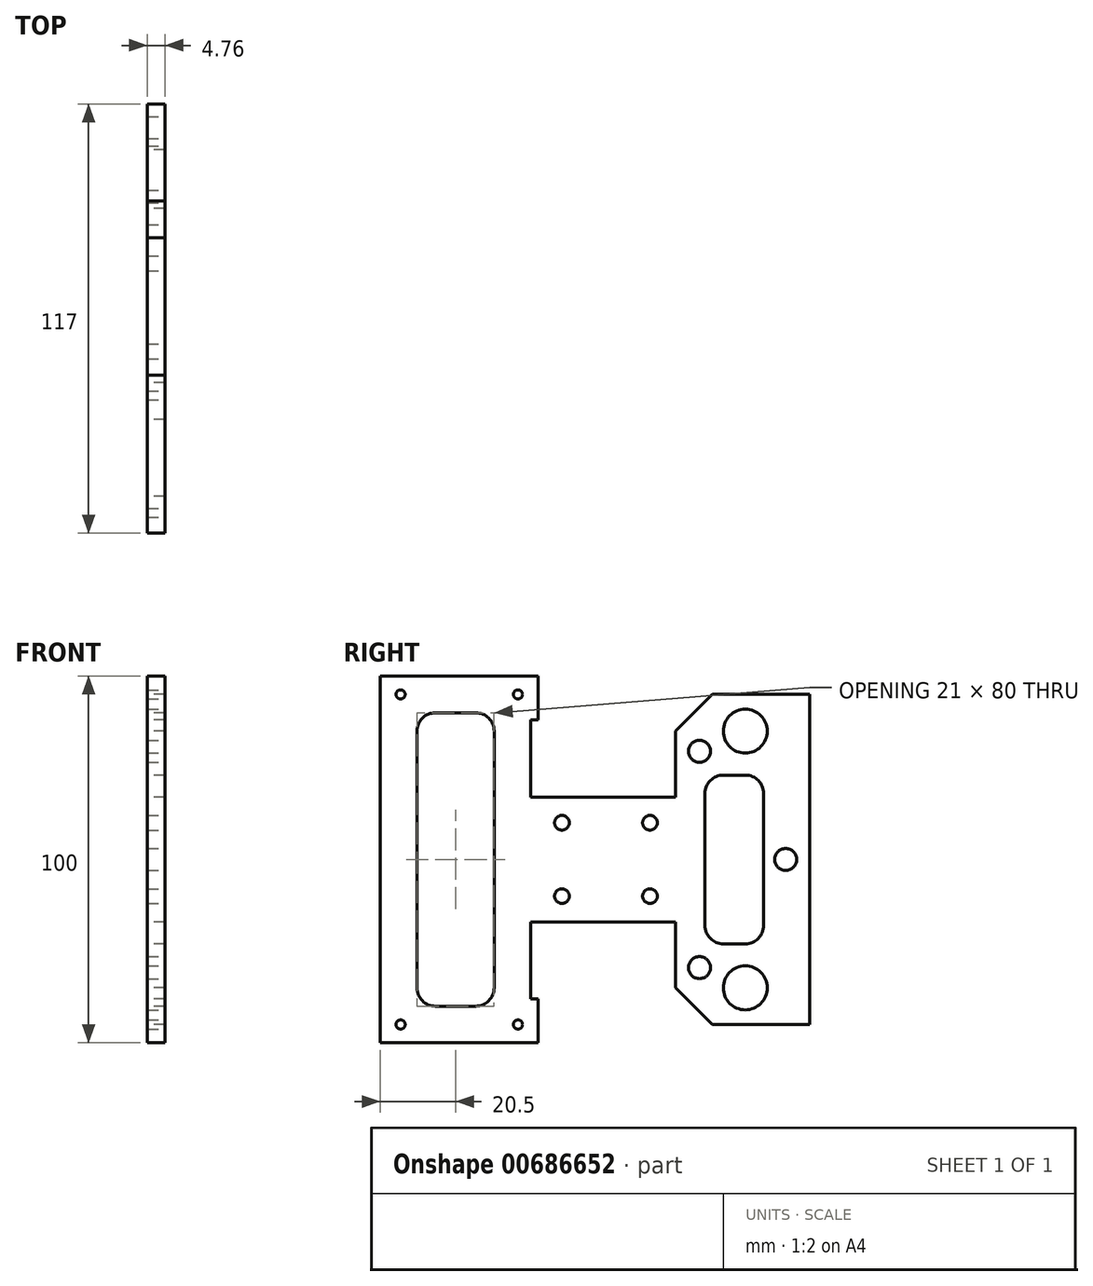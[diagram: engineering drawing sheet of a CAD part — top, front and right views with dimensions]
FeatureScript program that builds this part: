
annotation { "Feature Type Name" : "Feature", "Feature Type Description" : "" }
export const myFeature = defineFeature(function(context is Context, id is Id, definition is map)
    precondition{}
    {
        {
            var Q0;
            Q0=qCreatedBy(makeId("Right.planeOp"),FACE);
            var sketch = newSketch(context, id + "F0", { "sketchPlane" : qUnion([Q0])});
            skLineSegment(sketch, "E0.bottom", {"start": v(58.5, 17) * mm, "end": v(-58.5, 17) * mm});
            skLineSegment(sketch, "E0.top", {"start": v(58.5, -17) * mm, "end": v(-58.5, -17) * mm});
            skLineSegment(sketch, "E0.left", {"start": v(58.5, 17) * mm, "end": v(58.5, -17) * mm});
            skLineSegment(sketch, "E0.right", {"start": v(-58.5, 17) * mm, "end": v(-58.5, -17) * mm});
            skPoint(sketch, "E0.middle", {"position": v(0, 0) * mm});
            skLineSegment(sketch, "E1.bottom", {"start": v(-58.5, 17) * mm, "end": v(-17.5, 17) * mm, "construction": true});
            skLineSegment(sketch, "E1.top", {"start": v(-58.5, 38) * mm, "end": v(-17.5, 38) * mm, "construction": true});
            skLineSegment(sketch, "E1.left", {"start": v(-58.5, 17) * mm, "end": v(-58.5, 38) * mm});
            skLineSegment(sketch, "E1.right", {"start": v(-17.5, 17) * mm, "end": v(-17.5, 38) * mm});
            skLineSegment(sketch, "E2.bottom", {"start": v(-17.5, 38) * mm, "end": v(-15.5, 38) * mm});
            skLineSegment(sketch, "E2.top", {"start": v(-58.5, 50) * mm, "end": v(-15.5, 50) * mm});
            skLineSegment(sketch, "E2.left", {"start": v(-58.5, 38) * mm, "end": v(-58.5, 50) * mm});
            skLineSegment(sketch, "E2.right", {"start": v(-15.5, 38) * mm, "end": v(-15.5, 50) * mm});
            skLineSegment(sketch, "E3.bottom", {"start": v(58.5, 17) * mm, "end": v(22, 17) * mm});
            skLineSegment(sketch, "E3.top", {"start": v(58.5, 45) * mm, "end": v(32, 45) * mm});
            skLineSegment(sketch, "E3.left", {"start": v(58.5, 17) * mm, "end": v(58.5, 45) * mm});
            skLineSegment(sketch, "E3.right", {"start": v(22, 17) * mm, "end": v(22, 35) * mm});
            skLineSegment(sketch, "E4", {"start": v(22, 35) * mm, "end": v(32, 45) * mm});
            skLineSegment(sketch, "E5.bottom", {"start": v(-48.5, 0) * mm, "end": v(-27.5, 0) * mm});
            skLineSegment(sketch, "E5.top", {"start": v(-43.5, 40) * mm, "end": v(-32.5, 40) * mm});
            skLineSegment(sketch, "E5.left", {"start": v(-48.5, 0) * mm, "end": v(-48.5, 35) * mm});
            skLineSegment(sketch, "E5.right", {"start": v(-27.5, 0) * mm, "end": v(-27.5, 35) * mm});
            skLineSegment(sketch, "E6.bottom", {"start": v(-53, 50) * mm, "end": v(-21, 50) * mm});
            skLineSegment(sketch, "E6.top", {"start": v(-53, 45) * mm, "end": v(-21, 45) * mm, "construction": true});
            skLineSegment(sketch, "E6.left", {"start": v(-53, 50) * mm, "end": v(-53, 45) * mm, "construction": true});
            skLineSegment(sketch, "E6.right", {"start": v(-21, 50) * mm, "end": v(-21, 45) * mm, "construction": true});
            skLineSegment(sketch, "E7.bottom", {"start": v(-9, 10) * mm, "end": v(15, 10) * mm, "construction": true});
            skLineSegment(sketch, "E7.top", {"start": v(-9, 0) * mm, "end": v(15, 0) * mm, "construction": true});
            skLineSegment(sketch, "E7.left", {"start": v(-9, 10) * mm, "end": v(-9, 0) * mm, "construction": true});
            skLineSegment(sketch, "E7.right", {"start": v(15, 10) * mm, "end": v(15, 0) * mm, "construction": true});
            skLineSegment(sketch, "E8.bottom", {"start": v(30, 0) * mm, "end": v(46, 0) * mm});
            skLineSegment(sketch, "E8.top", {"start": v(35, 23) * mm, "end": v(41, 23) * mm});
            skLineSegment(sketch, "E8.left", {"start": v(30, 0) * mm, "end": v(30, 18) * mm});
            skLineSegment(sketch, "E8.right", {"start": v(46, 0) * mm, "end": v(46, 18) * mm});
            skPoint(sketch, "E9", {"position": v(52, 0) * mm});
            skPoint(sketch, "E10", {"position": v(28.5, 29.5) * mm});
            skPoint(sketch, "E11", {"position": v(41, 35) * mm});
            skLineSegment(sketch, "E12.MirrorCS", {"start": v(-48.5, 0) * mm, "end": v(-48.5, -35) * mm});
            skLineSegment(sketch, "E13.MirrorCS", {"start": v(-27.5, 0) * mm, "end": v(-27.5, -35) * mm});
            skLineSegment(sketch, "E14.MirrorCS", {"start": v(-43.5, -40) * mm, "end": v(-32.5, -40) * mm});
            skLineSegment(sketch, "E15.MirrorCS", {"start": v(-53, -45) * mm, "end": v(-21, -45) * mm, "construction": true});
            skLineSegment(sketch, "E16.MirrorCS", {"start": v(-53, -50) * mm, "end": v(-53, -45) * mm, "construction": true});
            skLineSegment(sketch, "E17.MirrorCS", {"start": v(-21, -50) * mm, "end": v(-21, -45) * mm, "construction": true});
            skLineSegment(sketch, "E18.MirrorCS", {"start": v(-15.5, -38) * mm, "end": v(-15.5, -50) * mm});
            skLineSegment(sketch, "E19.MirrorCS", {"start": v(-17.5, -38) * mm, "end": v(-15.5, -38) * mm});
            skLineSegment(sketch, "E20.MirrorCS", {"start": v(-17.5, -17) * mm, "end": v(-17.5, -38) * mm});
            skLineSegment(sketch, "E21.MirrorCS", {"start": v(-53, -50) * mm, "end": v(-21, -50) * mm});
            skLineSegment(sketch, "E22.MirrorCS", {"start": v(-58.5, -50) * mm, "end": v(-15.5, -50) * mm});
            skLineSegment(sketch, "E23.MirrorCS", {"start": v(-58.5, -38) * mm, "end": v(-58.5, -50) * mm});
            skLineSegment(sketch, "E24.MirrorCS", {"start": v(-58.5, -17) * mm, "end": v(-58.5, -38) * mm});
            skLineSegment(sketch, "E25.MirrorCS", {"start": v(-9, -10) * mm, "end": v(15, -10) * mm, "construction": true});
            skLineSegment(sketch, "E26.MirrorCS", {"start": v(-9, -10) * mm, "end": v(-9, 0) * mm, "construction": true});
            skLineSegment(sketch, "E27.MirrorCS", {"start": v(15, -10) * mm, "end": v(15, 0) * mm, "construction": true});
            skLineSegment(sketch, "E28.MirrorCS", {"start": v(30, 0) * mm, "end": v(30, -18) * mm});
            skLineSegment(sketch, "E29.MirrorCS", {"start": v(35, -23) * mm, "end": v(41, -23) * mm});
            skLineSegment(sketch, "E30.MirrorCS", {"start": v(46, 0) * mm, "end": v(46, -18) * mm});
            skLineSegment(sketch, "E31.MirrorCS", {"start": v(22, -17) * mm, "end": v(22, -35) * mm});
            skLineSegment(sketch, "E32.MirrorCS", {"start": v(22, -35) * mm, "end": v(32, -45) * mm});
            skLineSegment(sketch, "E33.MirrorCS", {"start": v(58.5, -45) * mm, "end": v(32, -45) * mm});
            skLineSegment(sketch, "E34.MirrorCS", {"start": v(58.5, -17) * mm, "end": v(58.5, -45) * mm});
            skPoint(sketch, "E35.MirrorP", {"position": v(41, -35) * mm});
            skPoint(sketch, "E36.MirrorP", {"position": v(28.5, -29.5) * mm});
            skPoint(sketch, "E37.visualSharp", {"position": v(-48.5, -40) * mm});
            skArc(sketch, "E37.filletArc", {"start": v(-48.5, -35) * mm, "mid": v(-47.04, -38.54) * mm, "end": v(-43.5, -40) * mm});
            skPoint(sketch, "E38.visualSharp", {"position": v(-27.5, -40) * mm});
            skArc(sketch, "E38.filletArc", {"start": v(-32.5, -40) * mm, "mid": v(-28.96, -38.54) * mm, "end": v(-27.5, -35) * mm});
            skPoint(sketch, "E39.visualSharp", {"position": v(-27.5, 40) * mm});
            skArc(sketch, "E39.filletArc", {"start": v(-27.5, 35) * mm, "mid": v(-28.96, 38.54) * mm, "end": v(-32.5, 40) * mm});
            skPoint(sketch, "E40.visualSharp", {"position": v(-48.5, 40) * mm});
            skArc(sketch, "E40.filletArc", {"start": v(-43.5, 40) * mm, "mid": v(-47.04, 38.54) * mm, "end": v(-48.5, 35) * mm});
            skPoint(sketch, "E41.visualSharp", {"position": v(30, 23) * mm});
            skArc(sketch, "E41.filletArc", {"start": v(35, 23) * mm, "mid": v(31.46, 21.54) * mm, "end": v(30, 18) * mm});
            skPoint(sketch, "E42.visualSharp", {"position": v(46, 23) * mm});
            skArc(sketch, "E42.filletArc", {"start": v(46, 18) * mm, "mid": v(44.54, 21.54) * mm, "end": v(41, 23) * mm});
            skPoint(sketch, "E43.visualSharp", {"position": v(46, -23) * mm});
            skArc(sketch, "E43.filletArc", {"start": v(41, -23) * mm, "mid": v(44.54, -21.54) * mm, "end": v(46, -18) * mm});
            skPoint(sketch, "E44.visualSharp", {"position": v(30, -23) * mm});
            skArc(sketch, "E44.filletArc", {"start": v(30, -18) * mm, "mid": v(31.46, -21.54) * mm, "end": v(35, -23) * mm});
            skLineSegment(sketch, "E45.bottom", {"start": v(-37.9, -50) * mm, "end": v(-28.5, -50) * mm, "construction": true});
            skLineSegment(sketch, "E45.top", {"start": v(-37.9, -44) * mm, "end": v(-28.5, -44) * mm, "construction": true});
            skLineSegment(sketch, "E45.left", {"start": v(-37.9, -50) * mm, "end": v(-37.9, -44) * mm, "construction": true});
            skLineSegment(sketch, "E45.right", {"start": v(-28.5, -50) * mm, "end": v(-28.5, -44) * mm, "construction": true});
            skSolve(sketch);
        }
        {
            var Q0;
            Q0 = qSketchRegion(id + "F0", true);
            extrude(context, id + "F1", {"entities" : qUnion([Q0]), "depth" : 4.76 * mm, "offsetDistance" : 25 * mm});
        }
        {
            var Q0;
            Q0=sQuery(id+"F0.wireOp",VERTEX,"E6.left.end");
            var Q1;
            Q1=sQuery(id+"F0.wireOp",VERTEX,"E6.right.end");
            var Q2;
            Q2=sQuery(id+"F0.wireOp",VERTEX,"E15.MirrorCS.end");
            var Q3;
            Q3=sQuery(id+"F0.wireOp",VERTEX,"E15.MirrorCS.start");
            var Q4;
            Q4=makeQuery(id+"F1.opExtrude","SWEPT_BODY",BODY,{"disambiguationData":[OSD([sQuery(id+"F0.wireOp",EDGE,"E0.bottom"),sQuery(id+"F0.wireOp",EDGE,"E0.top"),sQuery(id+"F0.wireOp",EDGE,"E0.left"),sQuery(id+"F0.wireOp",EDGE,"E0.right"),sQuery(id+"F0.wireOp",EDGE,"E1.left"),sQuery(id+"F0.wireOp",EDGE,"E1.right"),sQuery(id+"F0.wireOp",EDGE,"E2.bottom"),sQuery(id+"F0.wireOp",EDGE,"E2.top"),sQuery(id+"F0.wireOp",EDGE,"E2.left"),sQuery(id+"F0.wireOp",EDGE,"E2.right"),sQuery(id+"F0.wireOp",EDGE,"E3.top"),sQuery(id+"F0.wireOp",EDGE,"E3.left"),sQuery(id+"F0.wireOp",EDGE,"E3.right"),sQuery(id+"F0.wireOp",EDGE,"E4"),sQuery(id+"F0.wireOp",EDGE,"E5.top"),sQuery(id+"F0.wireOp",EDGE,"E5.left"),sQuery(id+"F0.wireOp",EDGE,"E5.right"),sQuery(id+"F0.wireOp",EDGE,"E6.bottom"),sQuery(id+"F0.wireOp",EDGE,"E8.top"),sQuery(id+"F0.wireOp",EDGE,"E8.left"),sQuery(id+"F0.wireOp",EDGE,"E8.right"),sQuery(id+"F0.wireOp",EDGE,"E12.MirrorCS"),sQuery(id+"F0.wireOp",EDGE,"E13.MirrorCS"),sQuery(id+"F0.wireOp",EDGE,"E14.MirrorCS"),sQuery(id+"F0.wireOp",EDGE,"E18.MirrorCS"),sQuery(id+"F0.wireOp",EDGE,"E19.MirrorCS"),sQuery(id+"F0.wireOp",EDGE,"E20.MirrorCS"),sQuery(id+"F0.wireOp",EDGE,"E22.MirrorCS"),sQuery(id+"F0.wireOp",EDGE,"E23.MirrorCS"),sQuery(id+"F0.wireOp",EDGE,"E24.MirrorCS"),sQuery(id+"F0.wireOp",EDGE,"E28.MirrorCS"),sQuery(id+"F0.wireOp",EDGE,"E29.MirrorCS"),sQuery(id+"F0.wireOp",EDGE,"E30.MirrorCS"),sQuery(id+"F0.wireOp",EDGE,"E31.MirrorCS"),sQuery(id+"F0.wireOp",EDGE,"E32.MirrorCS"),sQuery(id+"F0.wireOp",EDGE,"E33.MirrorCS"),sQuery(id+"F0.wireOp",EDGE,"E34.MirrorCS"),sQuery(id+"F0.wireOp",EDGE,"E37.filletArc"),sQuery(id+"F0.wireOp",EDGE,"E38.filletArc"),sQuery(id+"F0.wireOp",EDGE,"E39.filletArc"),sQuery(id+"F0.wireOp",EDGE,"E40.filletArc"),sQuery(id+"F0.wireOp",EDGE,"E41.filletArc"),sQuery(id+"F0.wireOp",EDGE,"E42.filletArc"),sQuery(id+"F0.wireOp",EDGE,"E43.filletArc"),sQuery(id+"F0.wireOp",EDGE,"E44.filletArc")])]});
            hole(context, id + "F2", {"style" : HoleStyle.SIMPLE, "endStyle" : HoleEndStyle.THROUGH, "oppositeDirection" : true, "standardTappedOrClearance" : lookupTablePath({ "standard" : "ISO", "engagement" : "75%", "pitch" : "0.5 mm", "size" : "M3", "type" : "Tapped" }), "standardBlindInLast" : lookupTablePath({ "standard" : "ISO", "engagement" : "75%", "pitch" : "0.5 mm", "size" : "M3", "type" : "Tapped" }), "holeDiameter" : 2.5 * mm, "majorDiameter" : 3 * mm, "showTappedDepth" : true, "isTappedThrough" : true, "tappedDepth" : 12 * mm, "tapClearance" : 3, "locations" : qUnion([Q0, Q1, Q2, Q3]), "scope" : qUnion([Q4]), "startStyle" : HoleStartStyle.PART});
        }
        {
            var Q0;
            Q0=sQuery(id+"F0.wireOp",VERTEX,"E7.bottom.start");
            var Q1;
            Q1=sQuery(id+"F0.wireOp",VERTEX,"E7.right.start");
            var Q2;
            Q2=sQuery(id+"F0.wireOp",VERTEX,"E27.MirrorCS.start");
            var Q3;
            Q3=sQuery(id+"F0.wireOp",VERTEX,"E25.MirrorCS.start");
            var Q4;
            Q4=makeQuery(id+"F1.opExtrude","SWEPT_BODY",BODY,{"disambiguationData":[OSD([sQuery(id+"F0.wireOp",EDGE,"E0.bottom"),sQuery(id+"F0.wireOp",EDGE,"E0.top"),sQuery(id+"F0.wireOp",EDGE,"E0.left"),sQuery(id+"F0.wireOp",EDGE,"E0.right"),sQuery(id+"F0.wireOp",EDGE,"E1.left"),sQuery(id+"F0.wireOp",EDGE,"E1.right"),sQuery(id+"F0.wireOp",EDGE,"E2.bottom"),sQuery(id+"F0.wireOp",EDGE,"E2.top"),sQuery(id+"F0.wireOp",EDGE,"E2.left"),sQuery(id+"F0.wireOp",EDGE,"E2.right"),sQuery(id+"F0.wireOp",EDGE,"E3.top"),sQuery(id+"F0.wireOp",EDGE,"E3.left"),sQuery(id+"F0.wireOp",EDGE,"E3.right"),sQuery(id+"F0.wireOp",EDGE,"E4"),sQuery(id+"F0.wireOp",EDGE,"E5.top"),sQuery(id+"F0.wireOp",EDGE,"E5.left"),sQuery(id+"F0.wireOp",EDGE,"E5.right"),sQuery(id+"F0.wireOp",EDGE,"E6.bottom"),sQuery(id+"F0.wireOp",EDGE,"E8.top"),sQuery(id+"F0.wireOp",EDGE,"E8.left"),sQuery(id+"F0.wireOp",EDGE,"E8.right"),sQuery(id+"F0.wireOp",EDGE,"E12.MirrorCS"),sQuery(id+"F0.wireOp",EDGE,"E13.MirrorCS"),sQuery(id+"F0.wireOp",EDGE,"E14.MirrorCS"),sQuery(id+"F0.wireOp",EDGE,"E18.MirrorCS"),sQuery(id+"F0.wireOp",EDGE,"E19.MirrorCS"),sQuery(id+"F0.wireOp",EDGE,"E20.MirrorCS"),sQuery(id+"F0.wireOp",EDGE,"E22.MirrorCS"),sQuery(id+"F0.wireOp",EDGE,"E23.MirrorCS"),sQuery(id+"F0.wireOp",EDGE,"E24.MirrorCS"),sQuery(id+"F0.wireOp",EDGE,"E28.MirrorCS"),sQuery(id+"F0.wireOp",EDGE,"E29.MirrorCS"),sQuery(id+"F0.wireOp",EDGE,"E30.MirrorCS"),sQuery(id+"F0.wireOp",EDGE,"E31.MirrorCS"),sQuery(id+"F0.wireOp",EDGE,"E32.MirrorCS"),sQuery(id+"F0.wireOp",EDGE,"E33.MirrorCS"),sQuery(id+"F0.wireOp",EDGE,"E34.MirrorCS"),sQuery(id+"F0.wireOp",EDGE,"E37.filletArc"),sQuery(id+"F0.wireOp",EDGE,"E38.filletArc"),sQuery(id+"F0.wireOp",EDGE,"E39.filletArc"),sQuery(id+"F0.wireOp",EDGE,"E40.filletArc"),sQuery(id+"F0.wireOp",EDGE,"E41.filletArc"),sQuery(id+"F0.wireOp",EDGE,"E42.filletArc"),sQuery(id+"F0.wireOp",EDGE,"E43.filletArc"),sQuery(id+"F0.wireOp",EDGE,"E44.filletArc")])]});
            hole(context, id + "F3", {"style" : HoleStyle.SIMPLE, "endStyle" : HoleEndStyle.THROUGH, "oppositeDirection" : true, "standardTappedOrClearance" : lookupTablePath({ "standard" : "ISO", "size" : "4", "type" : "Drilled" }), "standardBlindInLast" : lookupTablePath({ "standard" : "ISO", "size" : "4", "type" : "Drilled" }), "holeDiameter" : 4 * mm, "majorDiameter" : 3 * mm, "isTappedThrough" : true, "tappedDepth" : 12 * mm, "tapClearance" : 3, "locations" : qUnion([Q0, Q1, Q2, Q3]), "scope" : qUnion([Q4]), "startStyle" : HoleStartStyle.PART});
        }
        {
            var Q0;
            Q0=sQuery(id+"F0.wireOp",VERTEX,"E9");
            var Q1;
            Q1=sQuery(id+"F0.wireOp",VERTEX,"E36.MirrorP");
            var Q2;
            Q2=sQuery(id+"F0.wireOp",VERTEX,"E10");
            var Q3;
            Q3=makeQuery(id+"F1.opExtrude","SWEPT_BODY",BODY,{"disambiguationData":[OSD([sQuery(id+"F0.wireOp",EDGE,"E0.bottom"),sQuery(id+"F0.wireOp",EDGE,"E0.top"),sQuery(id+"F0.wireOp",EDGE,"E0.left"),sQuery(id+"F0.wireOp",EDGE,"E0.right"),sQuery(id+"F0.wireOp",EDGE,"E1.left"),sQuery(id+"F0.wireOp",EDGE,"E1.right"),sQuery(id+"F0.wireOp",EDGE,"E2.bottom"),sQuery(id+"F0.wireOp",EDGE,"E2.top"),sQuery(id+"F0.wireOp",EDGE,"E2.left"),sQuery(id+"F0.wireOp",EDGE,"E2.right"),sQuery(id+"F0.wireOp",EDGE,"E3.top"),sQuery(id+"F0.wireOp",EDGE,"E3.left"),sQuery(id+"F0.wireOp",EDGE,"E3.right"),sQuery(id+"F0.wireOp",EDGE,"E4"),sQuery(id+"F0.wireOp",EDGE,"E5.top"),sQuery(id+"F0.wireOp",EDGE,"E5.left"),sQuery(id+"F0.wireOp",EDGE,"E5.right"),sQuery(id+"F0.wireOp",EDGE,"E6.bottom"),sQuery(id+"F0.wireOp",EDGE,"E8.top"),sQuery(id+"F0.wireOp",EDGE,"E8.left"),sQuery(id+"F0.wireOp",EDGE,"E8.right"),sQuery(id+"F0.wireOp",EDGE,"E12.MirrorCS"),sQuery(id+"F0.wireOp",EDGE,"E13.MirrorCS"),sQuery(id+"F0.wireOp",EDGE,"E14.MirrorCS"),sQuery(id+"F0.wireOp",EDGE,"E18.MirrorCS"),sQuery(id+"F0.wireOp",EDGE,"E19.MirrorCS"),sQuery(id+"F0.wireOp",EDGE,"E20.MirrorCS"),sQuery(id+"F0.wireOp",EDGE,"E22.MirrorCS"),sQuery(id+"F0.wireOp",EDGE,"E23.MirrorCS"),sQuery(id+"F0.wireOp",EDGE,"E24.MirrorCS"),sQuery(id+"F0.wireOp",EDGE,"E28.MirrorCS"),sQuery(id+"F0.wireOp",EDGE,"E29.MirrorCS"),sQuery(id+"F0.wireOp",EDGE,"E30.MirrorCS"),sQuery(id+"F0.wireOp",EDGE,"E31.MirrorCS"),sQuery(id+"F0.wireOp",EDGE,"E32.MirrorCS"),sQuery(id+"F0.wireOp",EDGE,"E33.MirrorCS"),sQuery(id+"F0.wireOp",EDGE,"E34.MirrorCS"),sQuery(id+"F0.wireOp",EDGE,"E37.filletArc"),sQuery(id+"F0.wireOp",EDGE,"E38.filletArc"),sQuery(id+"F0.wireOp",EDGE,"E39.filletArc"),sQuery(id+"F0.wireOp",EDGE,"E40.filletArc"),sQuery(id+"F0.wireOp",EDGE,"E41.filletArc"),sQuery(id+"F0.wireOp",EDGE,"E42.filletArc"),sQuery(id+"F0.wireOp",EDGE,"E43.filletArc"),sQuery(id+"F0.wireOp",EDGE,"E44.filletArc")])]});
            hole(context, id + "F4", {"style" : HoleStyle.SIMPLE, "endStyle" : HoleEndStyle.THROUGH, "oppositeDirection" : true, "standardTappedOrClearance" : lookupTablePath({ "standard" : "ISO", "size" : "6", "type" : "Drilled" }), "standardBlindInLast" : lookupTablePath({ "standard" : "ISO", "size" : "6", "type" : "Drilled" }), "holeDiameter" : 6 * mm, "majorDiameter" : 5 * mm, "isTappedThrough" : true, "tappedDepth" : 12 * mm, "tapClearance" : 3, "locations" : qUnion([Q0, Q1, Q2]), "scope" : qUnion([Q3]), "startStyle" : HoleStartStyle.PART});
        }
        {
            var Q0;
            Q0=sQuery(id+"F0.wireOp",VERTEX,"E11");
            var Q1;
            Q1=sQuery(id+"F0.wireOp",VERTEX,"E35.MirrorP");
            var Q2;
            Q2=makeQuery(id+"F1.opExtrude","SWEPT_BODY",BODY,{"disambiguationData":[OSD([sQuery(id+"F0.wireOp",EDGE,"E0.bottom"),sQuery(id+"F0.wireOp",EDGE,"E0.top"),sQuery(id+"F0.wireOp",EDGE,"E0.left"),sQuery(id+"F0.wireOp",EDGE,"E0.right"),sQuery(id+"F0.wireOp",EDGE,"E1.left"),sQuery(id+"F0.wireOp",EDGE,"E1.right"),sQuery(id+"F0.wireOp",EDGE,"E2.bottom"),sQuery(id+"F0.wireOp",EDGE,"E2.top"),sQuery(id+"F0.wireOp",EDGE,"E2.left"),sQuery(id+"F0.wireOp",EDGE,"E2.right"),sQuery(id+"F0.wireOp",EDGE,"E3.top"),sQuery(id+"F0.wireOp",EDGE,"E3.left"),sQuery(id+"F0.wireOp",EDGE,"E3.right"),sQuery(id+"F0.wireOp",EDGE,"E4"),sQuery(id+"F0.wireOp",EDGE,"E5.top"),sQuery(id+"F0.wireOp",EDGE,"E5.left"),sQuery(id+"F0.wireOp",EDGE,"E5.right"),sQuery(id+"F0.wireOp",EDGE,"E6.bottom"),sQuery(id+"F0.wireOp",EDGE,"E8.top"),sQuery(id+"F0.wireOp",EDGE,"E8.left"),sQuery(id+"F0.wireOp",EDGE,"E8.right"),sQuery(id+"F0.wireOp",EDGE,"E12.MirrorCS"),sQuery(id+"F0.wireOp",EDGE,"E13.MirrorCS"),sQuery(id+"F0.wireOp",EDGE,"E14.MirrorCS"),sQuery(id+"F0.wireOp",EDGE,"E18.MirrorCS"),sQuery(id+"F0.wireOp",EDGE,"E19.MirrorCS"),sQuery(id+"F0.wireOp",EDGE,"E20.MirrorCS"),sQuery(id+"F0.wireOp",EDGE,"E22.MirrorCS"),sQuery(id+"F0.wireOp",EDGE,"E23.MirrorCS"),sQuery(id+"F0.wireOp",EDGE,"E24.MirrorCS"),sQuery(id+"F0.wireOp",EDGE,"E28.MirrorCS"),sQuery(id+"F0.wireOp",EDGE,"E29.MirrorCS"),sQuery(id+"F0.wireOp",EDGE,"E30.MirrorCS"),sQuery(id+"F0.wireOp",EDGE,"E31.MirrorCS"),sQuery(id+"F0.wireOp",EDGE,"E32.MirrorCS"),sQuery(id+"F0.wireOp",EDGE,"E33.MirrorCS"),sQuery(id+"F0.wireOp",EDGE,"E34.MirrorCS"),sQuery(id+"F0.wireOp",EDGE,"E37.filletArc"),sQuery(id+"F0.wireOp",EDGE,"E38.filletArc"),sQuery(id+"F0.wireOp",EDGE,"E39.filletArc"),sQuery(id+"F0.wireOp",EDGE,"E40.filletArc"),sQuery(id+"F0.wireOp",EDGE,"E41.filletArc"),sQuery(id+"F0.wireOp",EDGE,"E42.filletArc"),sQuery(id+"F0.wireOp",EDGE,"E43.filletArc"),sQuery(id+"F0.wireOp",EDGE,"E44.filletArc")])]});
            hole(context, id + "F5", {"style" : HoleStyle.SIMPLE, "endStyle" : HoleEndStyle.THROUGH, "oppositeDirection" : true, "standardTappedOrClearance" : lookupTablePath({ "standard" : "ISO", "size" : "12", "type" : "Drilled" }), "standardBlindInLast" : lookupTablePath({ "standard" : "ISO", "size" : "12", "type" : "Drilled" }), "holeDiameter" : 12 * mm, "majorDiameter" : 5 * mm, "isTappedThrough" : true, "tappedDepth" : 12 * mm, "tapClearance" : 3, "locations" : qUnion([Q0, Q1]), "scope" : qUnion([Q2]), "startStyle" : HoleStartStyle.PART});
        }
    });
